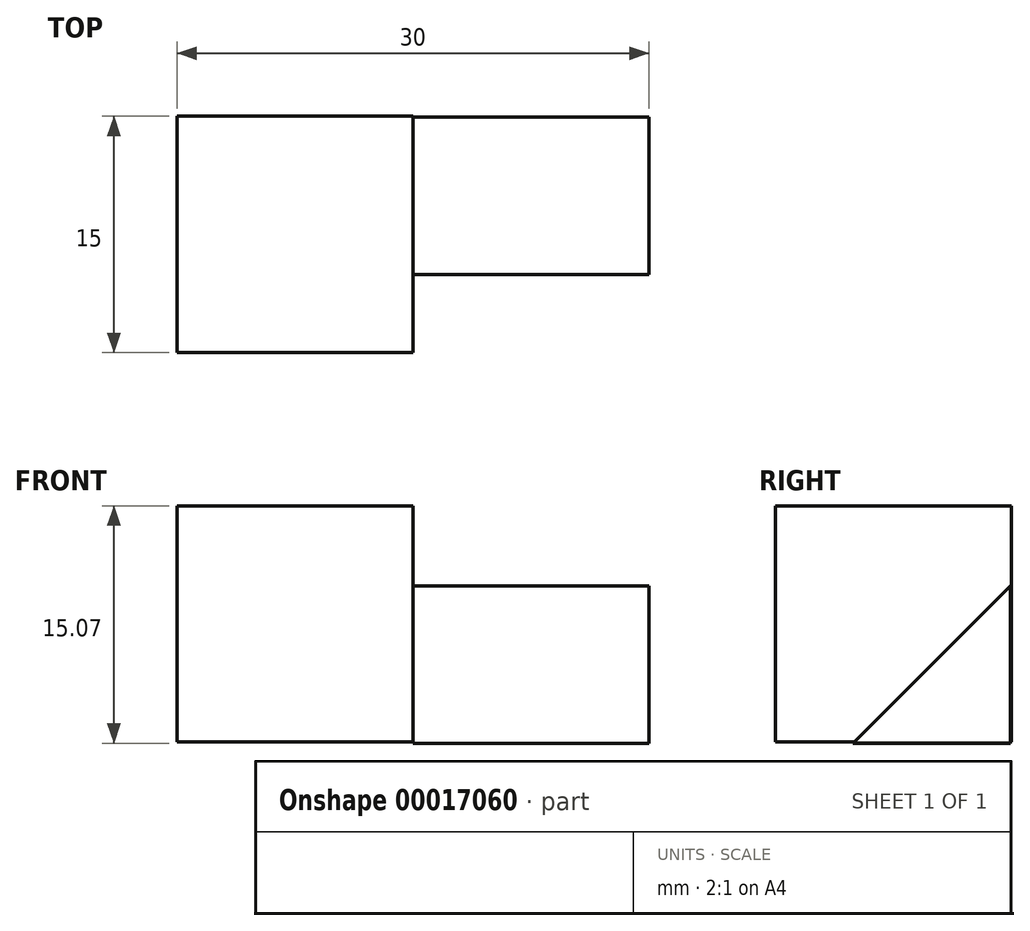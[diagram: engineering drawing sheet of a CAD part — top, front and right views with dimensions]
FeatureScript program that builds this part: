
annotation { "Feature Type Name" : "Feature", "Feature Type Description" : "" }
export const myFeature = defineFeature(function(context is Context, id is Id, definition is map)
    precondition{}
    {
        {
            var Q0;
            Q0=qCreatedBy(makeId("Right.planeOp"),FACE);
            var sketch = newSketch(context, id + "F0", { "sketchPlane" : qUnion([Q0])});
            skLineSegment(sketch, "E0.bottom", {"start": v(-3.53, 2.72) * mm, "end": v(11.47, 2.72) * mm});
            skLineSegment(sketch, "E0.top", {"start": v(-3.53, -12.28) * mm, "end": v(11.47, -12.28) * mm});
            skLineSegment(sketch, "E0.left", {"start": v(-3.53, 2.72) * mm, "end": v(-3.53, -12.28) * mm});
            skLineSegment(sketch, "E0.right", {"start": v(11.47, 2.72) * mm, "end": v(11.47, -12.28) * mm});
            skSolve(sketch);
        }
        {
            var Q0;
            Q0 = qSketchRegion(id + "F0", true);
            extrude(context, id + "F1", {"entities" : qUnion([Q0]), "oppositeDirection" : true, "depth" : 15 * mm});
        }
        {
            var Q0;
            Q0=qCreatedBy(makeId("Right.planeOp"),FACE);
            var sketch = newSketch(context, id + "F2", { "sketchPlane" : qUnion([Q0])});
            skLineSegment(sketch, "E1", {"start": v(11.41, -12.35) * mm, "end": v(1.41, -12.35) * mm});
            skLineSegment(sketch, "E2", {"start": v(11.41, -12.35) * mm, "end": v(11.41, -2.35) * mm});
            skLineSegment(sketch, "E3", {"start": v(11.41, -2.35) * mm, "end": v(1.41, -12.35) * mm});
            skSolve(sketch);
        }
        {
            var Q0;
            Q0 = qSketchRegion(id + "F2", true);
            extrude(context, id + "F3", {"entities" : qUnion([Q0]), "operationType" : NewBodyOperationType.ADD, "depth" : 15 * mm});
        }
    });
